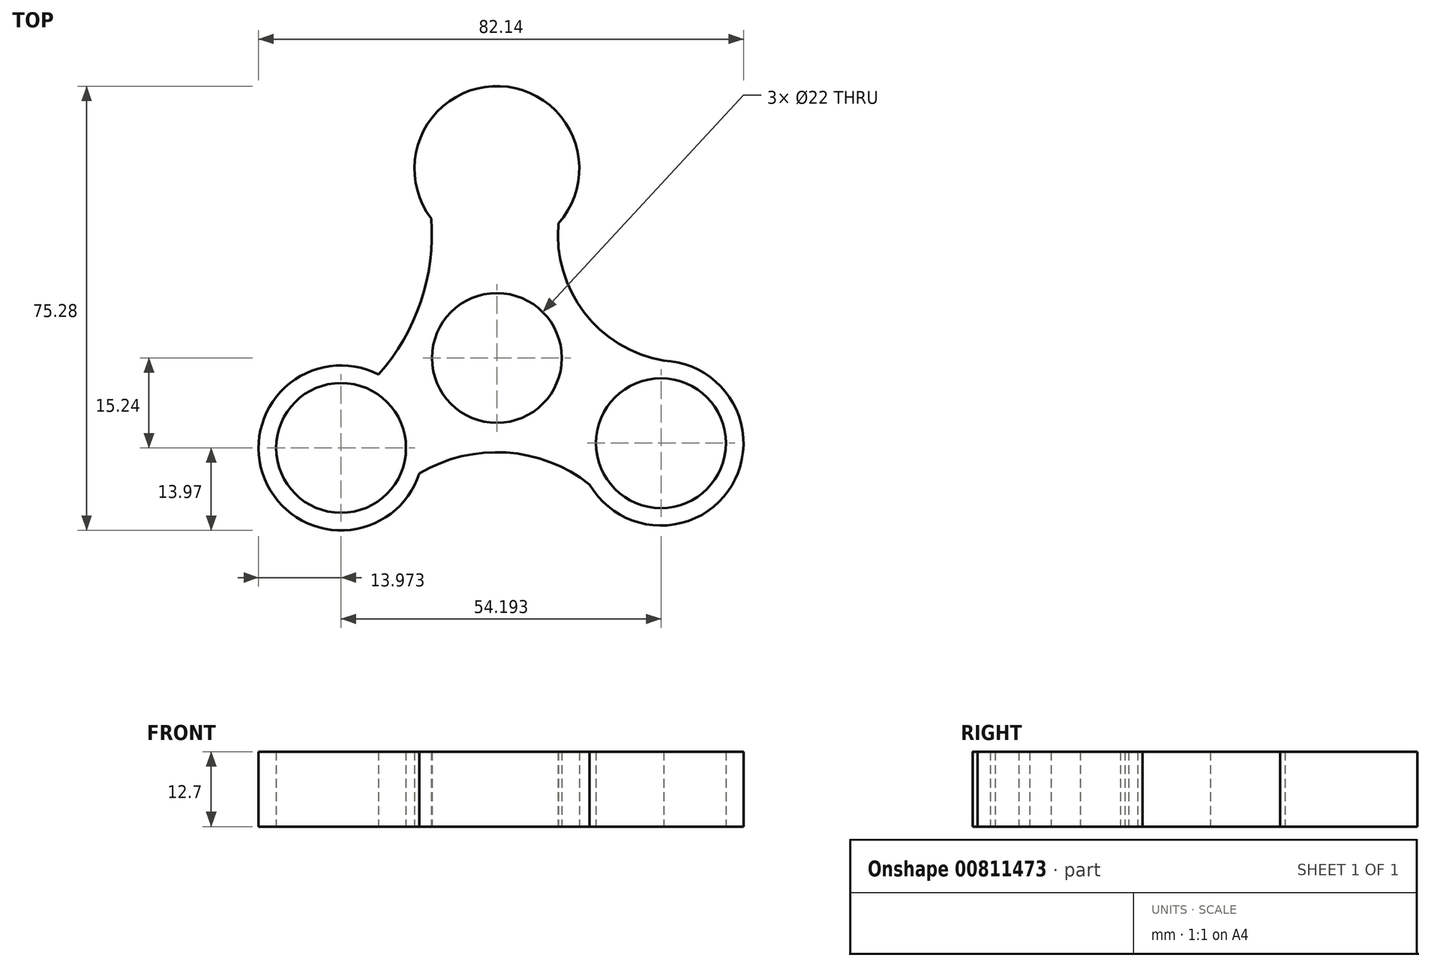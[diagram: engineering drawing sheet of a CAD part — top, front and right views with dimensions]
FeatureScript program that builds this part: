
annotation { "Feature Type Name" : "Feature", "Feature Type Description" : "" }
export const myFeature = defineFeature(function(context is Context, id is Id, definition is map)
    precondition{}
    {
        {
            var Q0;
            Q0=qCreatedBy(makeId("Top.planeOp"),FACE);
            var sketch = newSketch(context, id + "F0", { "sketchPlane" : qUnion([Q0])});
            skCircle(sketch, "E0", {"center": v(0, 0) * mm, "radius": 44.45 * mm});
            skCircle(sketch, "E1", {"center": v(0, 0) * mm, "radius": 11 * mm});
            skCircle(sketch, "E2", {"center": v(0, 32.1) * mm, "radius": 11 * mm});
            skCircle(sketch, "E3.1.0", {"center": v(-26.4, -15.24) * mm, "radius": 11 * mm});
            skCircle(sketch, "E3.2.0", {"center": v(27.8, -14.43) * mm, "radius": 11 * mm});
            skPoint(sketch, "E3.center", {"position": v(0.47, 0.8) * mm});
            skCircle(sketch, "E4", {"center": v(-26.4, -15.24) * mm, "radius": 13.97 * mm});
            skCircle(sketch, "E5", {"center": v(27.8, -14.43) * mm, "radius": 13.97 * mm});
            skCircle(sketch, "E6", {"center": v(0, 32.1) * mm, "radius": 13.97 * mm});
            skCircle(sketch, "E7", {"center": v(0, 0) * mm, "radius": 13.97 * mm});
            skArc(sketch, "E8", {"start": v(-20.03, -2.8) * mm, "mid": v(-12.9, 9.52) * mm, "end": v(-11.13, 23.66) * mm});
            skArc(sketch, "E9", {"start": v(15.71, -21.44) * mm, "mid": v(1.6, -16.03) * mm, "end": v(-13.11, -19.57) * mm});
            skArc(sketch, "E10", {"start": v(10.43, 22.8) * mm, "mid": v(14.79, 7.69) * mm, "end": v(28.25, -0.47) * mm});
            skSolve(sketch);
        }
        {
            var Q0;
            Q0=makeQuery(id+"F0.imprint","IMPRINT",FACE,{"disambiguationData":[TD([[makeQuery(id+"F0.imprint","IMPRINT",EDGE,{"derivedFrom":sQuery(id+"F0.wireOp",EDGE,"E1")}),-1.0]])]});
            var Q1;
            Q1=makeQuery(id+"F0.imprint","IMPRINT",FACE,{"disambiguationData":[TD([[makeQuery(id+"F0.imprint","IMPRINT",EDGE,{"derivedFrom":sQuery(id+"F0.wireOp",EDGE,"E3.1.0")}),-1.0]])]});
            var Q2;
            Q2=makeQuery(id+"F0.imprint","IMPRINT",FACE,{"disambiguationData":[TD([[makeQuery(id+"F0.imprint","IMPRINT",EDGE,{"derivedFrom":sQuery(id+"F0.wireOp",EDGE,"E3.2.0")}),-1.0]])]});
            var Q3;
            Q3=makeQuery(id+"F0.imprint","IMPRINT",FACE,{"disambiguationData":[TD([[makeQuery(id+"F0.imprint","IMPRINT",EDGE,{"derivedFrom":sQuery(id+"F0.wireOp",EDGE,"E7")}),-1.0]])]});
            var Q4;
            {var subQ0=sQuery(id+"F0.wireOp",EDGE,"E5");var subQ1=sQuery(id+"F0.wireOp",EDGE,"E0");var subQ2=makeQuery(id+"F0.imprint","INTERSECT",VERTEX,{"disambiguationData":[OD(0.0)],"derivedFrom":[subQ1,subQ0]});Q4=makeQuery(id+"F0.imprint","IMPRINT",FACE,{"disambiguationData":[TD([[makeQuery(id+"F0.imprint","IMPRINT",EDGE,{"disambiguationData":[TD([[subQ2,-1.0]])],"derivedFrom":subQ1}),-1.0]])]});}
            var Q5;
            Q5=makeQuery(id+"F0.imprint","IMPRINT",FACE,{"disambiguationData":[TD([[makeQuery(id+"F0.imprint","IMPRINT",EDGE,{"derivedFrom":sQuery(id+"F0.wireOp",EDGE,"E2")}),1.0]])]});
            var Q6;
            {var subQ0=sQuery(id+"F0.wireOp",EDGE,"E6");var subQ1=sQuery(id+"F0.wireOp",EDGE,"E0");var subQ2=makeQuery(id+"F0.imprint","INTERSECT",VERTEX,{"disambiguationData":[OD(0.0)],"derivedFrom":[subQ1,subQ0]});Q6=makeQuery(id+"F0.imprint","IMPRINT",FACE,{"disambiguationData":[TD([[makeQuery(id+"F0.imprint","IMPRINT",EDGE,{"disambiguationData":[TD([[subQ2,1.0]])],"derivedFrom":subQ1}),-1.0]])]});}
            var Q7;
            Q7=makeQuery(id+"F0.imprint","IMPRINT",FACE,{"disambiguationData":[TD([[makeQuery(id+"F0.imprint","IMPRINT",EDGE,{"derivedFrom":sQuery(id+"F0.wireOp",EDGE,"E2")}),-1.0]])]});
            extrude(context, id + "F1", {"entities" : qUnion([Q0, Q1, Q2, Q3, Q4, Q5, Q6, Q7]), "depth" : 12.7 * mm, "offsetDistance" : 25.4 * mm});
        }
    });
